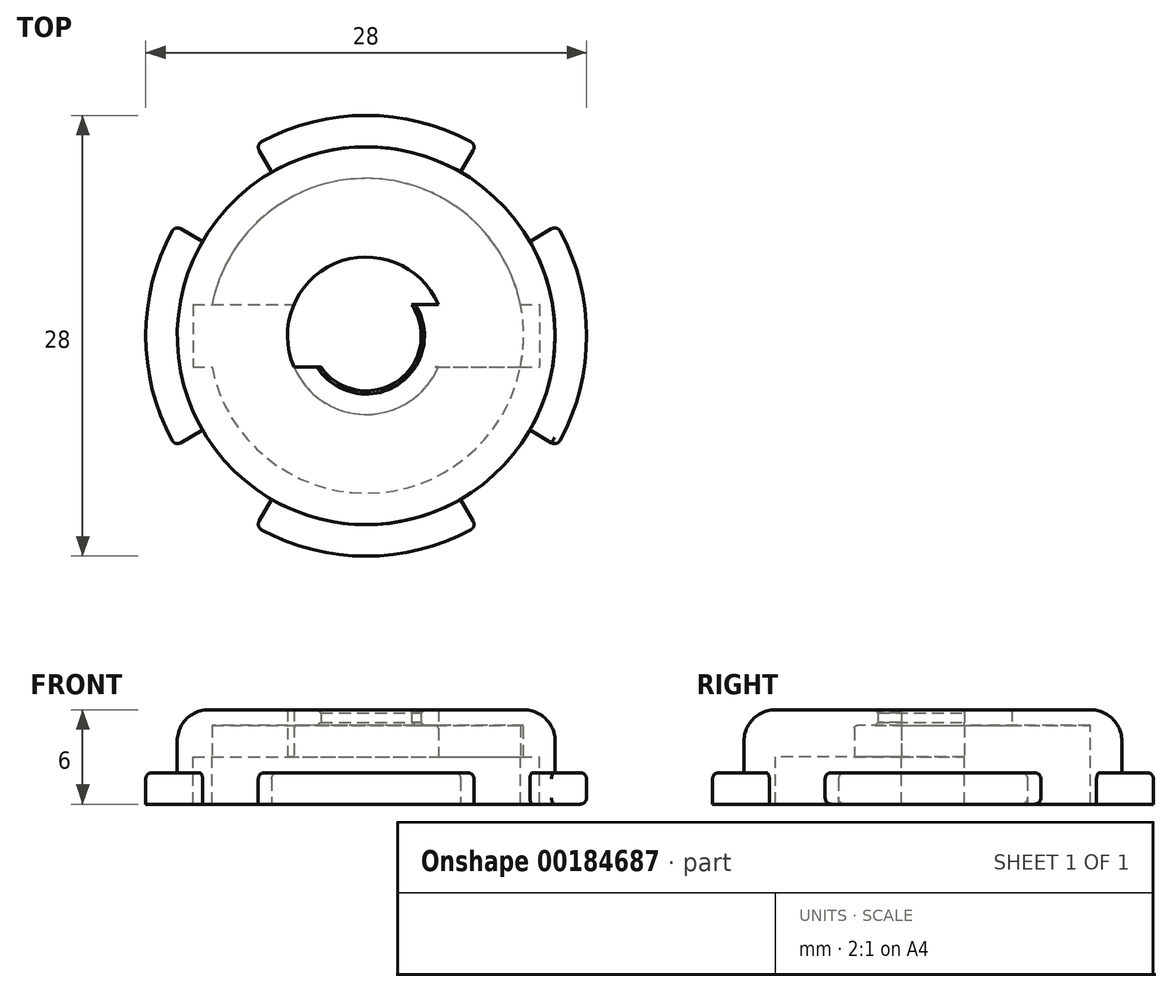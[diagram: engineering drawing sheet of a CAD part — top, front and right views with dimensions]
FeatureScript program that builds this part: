
annotation { "Feature Type Name" : "Feature", "Feature Type Description" : "" }
export const myFeature = defineFeature(function(context is Context, id is Id, definition is map)
    precondition{}
    {
        {
            var Q0;
            Q0=qCreatedBy(makeId("Top.planeOp"),FACE);
            var sketch = newSketch(context, id + "F0", { "sketchPlane" : qUnion([Q0])});
            skCircle(sketch, "E0", {"center": v(0, 0) * mm, "radius": 10 * mm});
            skLineSegment(sketch, "E1.bottom", {"start": v(-11, 2) * mm, "end": v(11, 2) * mm});
            skLineSegment(sketch, "E1.top", {"start": v(-11, -2) * mm, "end": v(11, -2) * mm});
            skLineSegment(sketch, "E1.left", {"start": v(-11, 2) * mm, "end": v(-11, -2) * mm});
            skLineSegment(sketch, "E1.right", {"start": v(11, 2) * mm, "end": v(11, -2) * mm});
            skCircle(sketch, "E2", {"center": v(0, 0) * mm, "radius": 12 * mm});
            skCircle(sketch, "E3", {"center": v(0, 0) * mm, "radius": 3.5 * mm});
            skCircle(sketch, "E4", {"center": v(0, 0) * mm, "radius": 5 * mm});
            skSolve(sketch);
        }
        {
            var Q0;
            {var subQ4=sQuery(id+"F0.wireOp",EDGE,"E1.left");Q0=makeQuery(id+"F0.imprint","IMPRINT",FACE,{"disambiguationData":[TD([[makeQuery(id+"F0.imprint","IMPRINT",EDGE,{"derivedFrom":subQ4}),-1.0]])]});}
            var Q1;
            {var subQ5=sQuery(id+"F0.wireOp",EDGE,"E1.left");Q1=makeQuery(id+"F0.imprint","IMPRINT",FACE,{"disambiguationData":[TD([[makeQuery(id+"F0.imprint","IMPRINT",EDGE,{"derivedFrom":subQ5}),1.0]])]});}
            var Q2;
            {var subQ0=sQuery(id+"F0.wireOp",EDGE,"E1.top");var subQ1=sQuery(id+"F0.wireOp",EDGE,"E0");var subQ2=makeQuery(id+"F0.imprint","INTERSECT",VERTEX,{"disambiguationData":[OD(0.0)],"derivedFrom":[subQ1,subQ0]});Q2=makeQuery(id+"F0.imprint","IMPRINT",FACE,{"disambiguationData":[TD([[makeQuery(id+"F0.imprint","IMPRINT",EDGE,{"disambiguationData":[TD([[subQ2,-1.0]])],"derivedFrom":subQ1}),1.0]])]});}
            var Q3;
            {var subQ0=sQuery(id+"F0.wireOp",EDGE,"E1.bottom");var subQ1=sQuery(id+"F0.wireOp",EDGE,"E0");var subQ2=makeQuery(id+"F0.imprint","INTERSECT",VERTEX,{"disambiguationData":[OD(0.0)],"derivedFrom":[subQ1,subQ0]});Q3=makeQuery(id+"F0.imprint","IMPRINT",FACE,{"disambiguationData":[TD([[makeQuery(id+"F0.imprint","IMPRINT",EDGE,{"disambiguationData":[TD([[subQ2,-1.0]])],"derivedFrom":subQ1}),1.0]])]});}
            var Q4;
            {var subQ0=sQuery(id+"F0.wireOp",EDGE,"E1.bottom");var subQ1=sQuery(id+"F0.wireOp",EDGE,"E0");var subQ2=makeQuery(id+"F0.imprint","INTERSECT",VERTEX,{"disambiguationData":[OD(0.0)],"derivedFrom":[subQ1,subQ0]});Q4=makeQuery(id+"F0.imprint","IMPRINT",FACE,{"disambiguationData":[TD([[makeQuery(id+"F0.imprint","IMPRINT",EDGE,{"disambiguationData":[TD([[subQ2,1.0]])],"derivedFrom":subQ1}),1.0]])]});}
            var Q5;
            {var subQ5=sQuery(id+"F0.wireOp",EDGE,"E1.right");Q5=makeQuery(id+"F0.imprint","IMPRINT",FACE,{"disambiguationData":[TD([[makeQuery(id+"F0.imprint","IMPRINT",EDGE,{"derivedFrom":subQ5}),-1.0]])]});}
            var Q6;
            {var subQ0=sQuery(id+"F0.wireOp",EDGE,"E1.bottom");var subQ1=sQuery(id+"F0.wireOp",EDGE,"E0");var subQ2=makeQuery(id+"F0.imprint","INTERSECT",VERTEX,{"disambiguationData":[OD(1.0)],"derivedFrom":[subQ1,subQ0]});Q6=makeQuery(id+"F0.imprint","IMPRINT",FACE,{"disambiguationData":[TD([[makeQuery(id+"F0.imprint","IMPRINT",EDGE,{"disambiguationData":[TD([[subQ2,1.0]])],"derivedFrom":subQ1}),1.0]])]});}
            var Q7;
            {var subQ0=sQuery(id+"F0.wireOp",EDGE,"E4");var subQ1=sQuery(id+"F0.wireOp",EDGE,"E1.top");var subQ2=makeQuery(id+"F0.imprint","INTERSECT",VERTEX,{"disambiguationData":[OD(0.0)],"derivedFrom":[subQ1,subQ0]});Q7=makeQuery(id+"F0.imprint","IMPRINT",FACE,{"disambiguationData":[TD([[makeQuery(id+"F0.imprint","IMPRINT",EDGE,{"disambiguationData":[TD([[subQ2,-1.0]])],"derivedFrom":subQ1}),-1.0]])]});}
            var Q8;
            {var subQ0=sQuery(id+"F0.wireOp",EDGE,"E4");var subQ1=sQuery(id+"F0.wireOp",EDGE,"E1.bottom");var subQ2=makeQuery(id+"F0.imprint","INTERSECT",VERTEX,{"disambiguationData":[OD(0.0)],"derivedFrom":[subQ1,subQ0]});Q8=makeQuery(id+"F0.imprint","IMPRINT",FACE,{"disambiguationData":[TD([[makeQuery(id+"F0.imprint","IMPRINT",EDGE,{"disambiguationData":[TD([[subQ2,-1.0]])],"derivedFrom":subQ1}),-1.0]])]});}
            var Q9;
            {var subQ0=sQuery(id+"F0.wireOp",EDGE,"E3");var subQ1=sQuery(id+"F0.wireOp",EDGE,"E1.top");var subQ2=makeQuery(id+"F0.imprint","INTERSECT",VERTEX,{"disambiguationData":[OD(0.0)],"derivedFrom":[subQ1,subQ0]});Q9=makeQuery(id+"F0.imprint","IMPRINT",FACE,{"disambiguationData":[TD([[makeQuery(id+"F0.imprint","IMPRINT",EDGE,{"disambiguationData":[TD([[subQ2,-1.0]])],"derivedFrom":subQ1}),-1.0]])]});}
            var Q10;
            {var subQ0=sQuery(id+"F0.wireOp",EDGE,"E3");var subQ1=sQuery(id+"F0.wireOp",EDGE,"E1.bottom");var subQ2=makeQuery(id+"F0.imprint","INTERSECT",VERTEX,{"disambiguationData":[OD(0.0)],"derivedFrom":[subQ1,subQ0]});Q10=makeQuery(id+"F0.imprint","IMPRINT",FACE,{"disambiguationData":[TD([[makeQuery(id+"F0.imprint","IMPRINT",EDGE,{"disambiguationData":[TD([[subQ2,-1.0]])],"derivedFrom":subQ1}),1.0]])]});}
            var Q11;
            {var subQ0=sQuery(id+"F0.wireOp",EDGE,"E4");var subQ1=sQuery(id+"F0.wireOp",EDGE,"E1.bottom");var subQ2=makeQuery(id+"F0.imprint","INTERSECT",VERTEX,{"disambiguationData":[OD(0.0)],"derivedFrom":[subQ1,subQ0]});Q11=makeQuery(id+"F0.imprint","IMPRINT",FACE,{"disambiguationData":[TD([[makeQuery(id+"F0.imprint","IMPRINT",EDGE,{"disambiguationData":[TD([[subQ2,-1.0]])],"derivedFrom":subQ1}),1.0]])]});}
            var Q12;
            {var subQ0=sQuery(id+"F0.wireOp",EDGE,"E3");var subQ1=sQuery(id+"F0.wireOp",EDGE,"E1.bottom");var subQ2=makeQuery(id+"F0.imprint","INTERSECT",VERTEX,{"disambiguationData":[OD(1.0)],"derivedFrom":[subQ1,subQ0]});Q12=makeQuery(id+"F0.imprint","IMPRINT",FACE,{"disambiguationData":[TD([[makeQuery(id+"F0.imprint","IMPRINT",EDGE,{"disambiguationData":[TD([[subQ2,-1.0]])],"derivedFrom":subQ1}),-1.0]])]});}
            var Q13;
            {var subQ0=sQuery(id+"F0.wireOp",EDGE,"E3");var subQ1=sQuery(id+"F0.wireOp",EDGE,"E1.bottom");var subQ2=makeQuery(id+"F0.imprint","INTERSECT",VERTEX,{"disambiguationData":[OD(0.0)],"derivedFrom":[subQ1,subQ0]});Q13=makeQuery(id+"F0.imprint","IMPRINT",FACE,{"disambiguationData":[TD([[makeQuery(id+"F0.imprint","IMPRINT",EDGE,{"disambiguationData":[TD([[subQ2,-1.0]])],"derivedFrom":subQ1}),-1.0]])]});}
            extrude(context, id + "F1", {"entities" : qUnion([Q0, Q1, Q2, Q3, Q4, Q5, Q6, Q7, Q8, Q9, Q10, Q11, Q12, Q13]), "depth" : 3 * mm});
        }
        {
            var Q0;
            {var subQ4=sQuery(id+"F0.wireOp",EDGE,"E1.left");Q0=makeQuery(id+"F0.imprint","IMPRINT",FACE,{"disambiguationData":[TD([[makeQuery(id+"F0.imprint","IMPRINT",EDGE,{"derivedFrom":subQ4}),-1.0]])]});}
            extrude(context, id + "F2", {"entities" : qUnion([Q0]), "operationType" : NewBodyOperationType.ADD, "oppositeDirection" : true, "depth" : 3 * mm});
        }
        {
            var Q0;
            Q0=makeQuery(id+"F1.opExtrude","CAP_EDGE",EDGE,{"disambiguationData":[OSD([sQuery(id+"F0.wireOp",EDGE,"E2")])],"isStart":false});
            fillet(context, id + "F3", {"entities" : qUnion([Q0]), "radius" : 2 * mm, "tangentPropagation" : true, "allowEdgeOverflow" : false});
        }
        {
            var Q0;
            Q0=qCreatedBy(makeId("Top.planeOp"),FACE);
            var sketch = newSketch(context, id + "F4", { "sketchPlane" : qUnion([Q0])});
            skLineSegment(sketch, "E5.bottom", {"start": v(-6.5, -2) * mm, "end": v(-3.5, -2) * mm});
            skLineSegment(sketch, "E5.top", {"start": v(-6.5, 2) * mm, "end": v(-3.5, 2) * mm});
            skLineSegment(sketch, "E5.left", {"start": v(-6.5, -2) * mm, "end": v(-6.5, 2) * mm});
            skLineSegment(sketch, "E5.right", {"start": v(-3.5, -2) * mm, "end": v(-3.5, 2) * mm});
            skLineSegment(sketch, "E6.bottom", {"start": v(3.5, -2) * mm, "end": v(6.5, -2) * mm});
            skLineSegment(sketch, "E6.top", {"start": v(3.5, 2) * mm, "end": v(6.5, 2) * mm});
            skLineSegment(sketch, "E6.left", {"start": v(3.5, -2) * mm, "end": v(3.5, 2) * mm});
            skLineSegment(sketch, "E6.right", {"start": v(6.5, -2) * mm, "end": v(6.5, 2) * mm});
            skCircle(sketch, "E7", {"center": v(0, 0) * mm, "radius": 9.5 * mm});
            skCircle(sketch, "E8", {"center": v(0, 0) * mm, "radius": 5 * mm});
            skSolve(sketch);
        }
        {
            var Q0;
            {var subQ0=sQuery(id+"F0.wireOp",EDGE,"E4");var subQ1=sQuery(id+"F0.wireOp",EDGE,"E1.top");var subQ2=makeQuery(id+"F0.imprint","INTERSECT",VERTEX,{"disambiguationData":[OD(0.0)],"derivedFrom":[subQ1,subQ0]});Q0=makeQuery(id+"F0.imprint","IMPRINT",FACE,{"disambiguationData":[TD([[makeQuery(id+"F0.imprint","IMPRINT",EDGE,{"disambiguationData":[TD([[subQ2,-1.0]])],"derivedFrom":subQ1}),-1.0]])]});}
            var Q1;
            {var subQ0=sQuery(id+"F0.wireOp",EDGE,"E3");var subQ1=sQuery(id+"F0.wireOp",EDGE,"E1.bottom");var subQ2=makeQuery(id+"F0.imprint","INTERSECT",VERTEX,{"disambiguationData":[OD(1.0)],"derivedFrom":[subQ1,subQ0]});Q1=makeQuery(id+"F0.imprint","IMPRINT",FACE,{"disambiguationData":[TD([[makeQuery(id+"F0.imprint","IMPRINT",EDGE,{"disambiguationData":[TD([[subQ2,-1.0]])],"derivedFrom":subQ1}),-1.0]])]});}
            var Q2;
            {var subQ0=sQuery(id+"F0.wireOp",EDGE,"E4");var subQ1=sQuery(id+"F0.wireOp",EDGE,"E1.bottom");var subQ2=makeQuery(id+"F0.imprint","INTERSECT",VERTEX,{"disambiguationData":[OD(0.0)],"derivedFrom":[subQ1,subQ0]});Q2=makeQuery(id+"F0.imprint","IMPRINT",FACE,{"disambiguationData":[TD([[makeQuery(id+"F0.imprint","IMPRINT",EDGE,{"disambiguationData":[TD([[subQ2,-1.0]])],"derivedFrom":subQ1}),1.0]])]});}
            var Q3;
            {var subQ0=sQuery(id+"F0.wireOp",EDGE,"E4");var subQ1=sQuery(id+"F0.wireOp",EDGE,"E1.bottom");var subQ2=makeQuery(id+"F0.imprint","INTERSECT",VERTEX,{"disambiguationData":[OD(0.0)],"derivedFrom":[subQ1,subQ0]});Q3=makeQuery(id+"F0.imprint","IMPRINT",FACE,{"disambiguationData":[TD([[makeQuery(id+"F0.imprint","IMPRINT",EDGE,{"disambiguationData":[TD([[subQ2,-1.0]])],"derivedFrom":subQ1}),-1.0]])]});}
            var Q4;
            {var subQ0=sQuery(id+"F0.wireOp",EDGE,"E3");var subQ1=sQuery(id+"F0.wireOp",EDGE,"E1.bottom");var subQ2=makeQuery(id+"F0.imprint","INTERSECT",VERTEX,{"disambiguationData":[OD(0.0)],"derivedFrom":[subQ1,subQ0]});Q4=makeQuery(id+"F0.imprint","IMPRINT",FACE,{"disambiguationData":[TD([[makeQuery(id+"F0.imprint","IMPRINT",EDGE,{"disambiguationData":[TD([[subQ2,-1.0]])],"derivedFrom":subQ1}),1.0]])]});}
            var Q5;
            {var subQ0=sQuery(id+"F4.wireOp",EDGE,"E5.right");Q5=makeQuery(id+"F4.imprint","IMPRINT",FACE,{"disambiguationData":[TD([[makeQuery(id+"F4.imprint","IMPRINT",EDGE,{"derivedFrom":subQ0}),1.0]])]});}
            var Q6;
            {var subQ0=sQuery(id+"F0.wireOp",EDGE,"E3");var subQ1=sQuery(id+"F0.wireOp",EDGE,"E1.top");var subQ2=makeQuery(id+"F0.imprint","INTERSECT",VERTEX,{"disambiguationData":[OD(0.0)],"derivedFrom":[subQ1,subQ0]});Q6=makeQuery(id+"F0.imprint","IMPRINT",FACE,{"disambiguationData":[TD([[makeQuery(id+"F0.imprint","IMPRINT",EDGE,{"disambiguationData":[TD([[subQ2,-1.0]])],"derivedFrom":subQ1}),-1.0]])]});}
            var Q7;
            {var subQ0=sQuery(id+"F4.wireOp",EDGE,"E6.left");Q7=makeQuery(id+"F4.imprint","IMPRINT",FACE,{"disambiguationData":[TD([[makeQuery(id+"F4.imprint","IMPRINT",EDGE,{"derivedFrom":subQ0}),-1.0]])]});}
            var Q8;
            {var subQ0=sQuery(id+"F0.wireOp",EDGE,"E3");var subQ1=sQuery(id+"F0.wireOp",EDGE,"E1.bottom");var subQ2=makeQuery(id+"F0.imprint","INTERSECT",VERTEX,{"disambiguationData":[OD(0.0)],"derivedFrom":[subQ1,subQ0]});Q8=makeQuery(id+"F0.imprint","IMPRINT",FACE,{"disambiguationData":[TD([[makeQuery(id+"F0.imprint","IMPRINT",EDGE,{"disambiguationData":[TD([[subQ2,-1.0]])],"derivedFrom":subQ1}),-1.0]])]});}
            extrude(context, id + "F5", {"entities" : qUnion([Q0, Q1, Q2, Q3, Q4, Q5, Q6, Q7, Q8]), "operationType" : NewBodyOperationType.REMOVE, "depth" : 2 * mm});
        }
        {
            var Q0;
            Q0=makeQuery(id+"F2.opExtrude","CAP_FACE",FACE,{"disambiguationData":[OSD([sQuery(id+"F0.wireOp",EDGE,"E0"),sQuery(id+"F0.wireOp",EDGE,"E1.bottom"),sQuery(id+"F0.wireOp",EDGE,"E1.top"),sQuery(id+"F0.wireOp",EDGE,"E1.left"),sQuery(id+"F0.wireOp",EDGE,"E1.right"),sQuery(id+"F0.wireOp",EDGE,"E2")])],"isStart":false});
            var sketch = newSketch(context, id + "F6", { "sketchPlane" : qUnion([Q0])});
            skCircle(sketch, "E9", {"center": v(0, 0) * mm, "radius": 14 * mm});
            skLineSegment(sketch, "E10", {"start": v(0, 0) * mm, "end": v(-12.12, -7) * mm});
            skLineSegment(sketch, "E11", {"start": v(-7, -12.12) * mm, "end": v(0, 0) * mm});
            skPoint(sketch, "E12.orphan", {"position": v(14.5, 8.38) * mm});
            skPoint(sketch, "E13.orphan", {"position": v(8.38, -14.5) * mm});
            skPoint(sketch, "E14.orphan", {"position": v(-8.2, -14.2) * mm});
            skPoint(sketch, "E15.orphan", {"position": v(-14.5, -8.38) * mm});
            skPoint(sketch, "E16.orphan", {"position": v(-14.2, 8.2) * mm});
            skCircle(sketch, "E17", {"center": v(0, 0) * mm, "radius": 16 * mm});
            skCircle(sketch, "E18", {"center": v(0, 0) * mm, "radius": 12 * mm});
            skLineSegment(sketch, "E19.1.0", {"start": v(12.12, -7) * mm, "end": v(0, 0) * mm});
            skLineSegment(sketch, "E19.1.1", {"start": v(0, 0) * mm, "end": v(7, -12.12) * mm});
            skLineSegment(sketch, "E19.2.0", {"start": v(7, 12.12) * mm, "end": v(0, 0) * mm});
            skLineSegment(sketch, "E19.2.1", {"start": v(0, 0) * mm, "end": v(12.12, 7) * mm});
            skLineSegment(sketch, "E19.3.0", {"start": v(-12.12, 7) * mm, "end": v(0, 0) * mm});
            skLineSegment(sketch, "E19.3.1", {"start": v(0, 0) * mm, "end": v(-7, 12.12) * mm});
            skSolve(sketch);
        }
        {
            var Q0;
            {var subQ0=sQuery(id+"F6.wireOp",EDGE,"E10");var subQ1=sQuery(id+"F6.wireOp",EDGE,"E9");var subQ2=makeQuery(id+"F6.imprint","INTERSECT",VERTEX,{"derivedFrom":[subQ1,subQ0]});Q0=makeQuery(id+"F6.imprint","IMPRINT",FACE,{"disambiguationData":[TD([[makeQuery(id+"F6.imprint","IMPRINT",EDGE,{"disambiguationData":[TD([[subQ2,1.0]])],"derivedFrom":subQ1}),1.0]])]});}
            var Q1;
            {var subQ0=sQuery(id+"F6.wireOp",EDGE,"E19.2.0");var subQ1=sQuery(id+"F6.wireOp",EDGE,"E9");var subQ2=makeQuery(id+"F6.imprint","INTERSECT",VERTEX,{"derivedFrom":[subQ1,subQ0]});Q1=makeQuery(id+"F6.imprint","IMPRINT",FACE,{"disambiguationData":[TD([[makeQuery(id+"F6.imprint","IMPRINT",EDGE,{"disambiguationData":[TD([[subQ2,-1.0]])],"derivedFrom":subQ1}),1.0]])]});}
            var Q2;
            {var subQ0=sQuery(id+"F6.wireOp",EDGE,"E19.1.0");var subQ1=sQuery(id+"F6.wireOp",EDGE,"E9");var subQ2=makeQuery(id+"F6.imprint","INTERSECT",VERTEX,{"derivedFrom":[subQ1,subQ0]});Q2=makeQuery(id+"F6.imprint","IMPRINT",FACE,{"disambiguationData":[TD([[makeQuery(id+"F6.imprint","IMPRINT",EDGE,{"disambiguationData":[TD([[subQ2,-1.0]])],"derivedFrom":subQ1}),1.0]])]});}
            var Q3;
            {var subQ0=sQuery(id+"F6.wireOp",EDGE,"E11");var subQ1=sQuery(id+"F6.wireOp",EDGE,"E9");var subQ2=makeQuery(id+"F6.imprint","INTERSECT",VERTEX,{"derivedFrom":[subQ1,subQ0]});Q3=makeQuery(id+"F6.imprint","IMPRINT",FACE,{"disambiguationData":[TD([[makeQuery(id+"F6.imprint","IMPRINT",EDGE,{"disambiguationData":[TD([[subQ2,-1.0]])],"derivedFrom":subQ1}),1.0]])]});}
            extrude(context, id + "F7", {"entities" : qUnion([Q0, Q1, Q2, Q3]), "operationType" : NewBodyOperationType.ADD, "oppositeDirection" : true, "depth" : 2 * mm});
        }
        {
            var Q0;
            Q0=makeQuery(id+"F7.opExtrude","SWEPT_EDGE",EDGE,{"disambiguationData":[OSD([sQuery(id+"F6.wireOp",EDGE,"E18"),sQuery(id+"F6.wireOp",EDGE,"E19.2.1")])]});
            var Q1;
            Q1=makeQuery(id+"F7.opExtrude","SWEPT_EDGE",EDGE,{"disambiguationData":[OSD([sQuery(id+"F6.wireOp",EDGE,"E18"),sQuery(id+"F6.wireOp",EDGE,"E19.2.0")])]});
            var Q2;
            Q2=makeQuery(id+"F7.opExtrude","SWEPT_EDGE",EDGE,{"disambiguationData":[OSD([sQuery(id+"F6.wireOp",EDGE,"E9"),sQuery(id+"F6.wireOp",EDGE,"E19.2.1")])]});
            var Q3;
            Q3=makeQuery(id+"F7.opExtrude","SWEPT_EDGE",EDGE,{"disambiguationData":[OSD([sQuery(id+"F6.wireOp",EDGE,"E9"),sQuery(id+"F6.wireOp",EDGE,"E19.2.0")])]});
            var Q4;
            Q4=makeQuery(id+"F7.opExtrude","SWEPT_EDGE",EDGE,{"disambiguationData":[OSD([sQuery(id+"F6.wireOp",EDGE,"E9"),sQuery(id+"F6.wireOp",EDGE,"E19.3.1")])]});
            var Q5;
            Q5=makeQuery(id+"F7.opExtrude","SWEPT_EDGE",EDGE,{"disambiguationData":[OSD([sQuery(id+"F6.wireOp",EDGE,"E9"),sQuery(id+"F6.wireOp",EDGE,"E19.3.0")])]});
            var Q6;
            Q6=makeQuery(id+"F7.opExtrude","SWEPT_EDGE",EDGE,{"disambiguationData":[OSD([sQuery(id+"F6.wireOp",EDGE,"E18"),sQuery(id+"F6.wireOp",EDGE,"E19.3.1")])]});
            var Q7;
            Q7=makeQuery(id+"F7.opExtrude","SWEPT_EDGE",EDGE,{"disambiguationData":[OSD([sQuery(id+"F6.wireOp",EDGE,"E18"),sQuery(id+"F6.wireOp",EDGE,"E19.3.0")])]});
            var Q8;
            Q8=makeQuery(id+"F7.opExtrude","SWEPT_EDGE",EDGE,{"disambiguationData":[OSD([sQuery(id+"F6.wireOp",EDGE,"E10"),sQuery(id+"F6.wireOp",EDGE,"E18")])]});
            var Q9;
            Q9=makeQuery(id+"F7.opExtrude","SWEPT_EDGE",EDGE,{"disambiguationData":[OSD([sQuery(id+"F6.wireOp",EDGE,"E9"),sQuery(id+"F6.wireOp",EDGE,"E10")])]});
            var Q10;
            Q10=makeQuery(id+"F7.opExtrude","SWEPT_EDGE",EDGE,{"disambiguationData":[OSD([sQuery(id+"F6.wireOp",EDGE,"E11"),sQuery(id+"F6.wireOp",EDGE,"E18")])]});
            var Q11;
            Q11=makeQuery(id+"F7.opExtrude","SWEPT_EDGE",EDGE,{"disambiguationData":[OSD([sQuery(id+"F6.wireOp",EDGE,"E9"),sQuery(id+"F6.wireOp",EDGE,"E11")])]});
            var Q12;
            Q12=makeQuery(id+"F7.opExtrude","SWEPT_EDGE",EDGE,{"disambiguationData":[OSD([sQuery(id+"F6.wireOp",EDGE,"E18"),sQuery(id+"F6.wireOp",EDGE,"E19.1.1")])]});
            var Q13;
            Q13=makeQuery(id+"F7.opExtrude","SWEPT_EDGE",EDGE,{"disambiguationData":[OSD([sQuery(id+"F6.wireOp",EDGE,"E9"),sQuery(id+"F6.wireOp",EDGE,"E19.1.1")])]});
            var Q14;
            Q14=makeQuery(id+"F7.opExtrude","SWEPT_EDGE",EDGE,{"disambiguationData":[OSD([sQuery(id+"F6.wireOp",EDGE,"E18"),sQuery(id+"F6.wireOp",EDGE,"E19.1.0")])]});
            var Q15;
            Q15=makeQuery(id+"F7.opExtrude","SWEPT_EDGE",EDGE,{"disambiguationData":[OSD([sQuery(id+"F6.wireOp",EDGE,"E9"),sQuery(id+"F6.wireOp",EDGE,"E19.1.0")])]});
            fillet(context, id + "F8", {"entities" : qUnion([Q0, Q1, Q2, Q3, Q4, Q5, Q6, Q7, Q8, Q9, Q10, Q11, Q12, Q13, Q14, Q15]), "radius" : 0.4 * mm, "tangentPropagation" : true, "allowEdgeOverflow" : false});
        }
        {
            var Q0;
            {var subQ0=sQuery(id+"F6.wireOp",EDGE,"E9");Q0=makeQuery(id+"F7.opExtrude","CAP_EDGE",EDGE,{"disambiguationData":[OSD([subQ0]),TDD([makeQuery(id+"F6.imprint","IMPRINT",EDGE,{"disambiguationData":[TD([[makeQuery(id+"F6.imprint","INTERSECT",VERTEX,{"derivedFrom":[subQ0,sQuery(id+"F6.wireOp",EDGE,"E19.1.0")]}),-1.0]])],"derivedFrom":subQ0})])],"isStart":true});}
            var Q1;
            {var subQ0=sQuery(id+"F6.wireOp",EDGE,"E9");Q1=makeQuery(id+"F7.opExtrude","CAP_EDGE",EDGE,{"disambiguationData":[OSD([subQ0]),TDD([makeQuery(id+"F6.imprint","IMPRINT",EDGE,{"disambiguationData":[TD([[makeQuery(id+"F6.imprint","INTERSECT",VERTEX,{"derivedFrom":[subQ0,sQuery(id+"F6.wireOp",EDGE,"E19.1.0")]}),-1.0]])],"derivedFrom":subQ0})])],"isStart":false});}
            var Q2;
            {var subQ0=sQuery(id+"F6.wireOp",EDGE,"E9");Q2=makeQuery(id+"F7.opExtrude","CAP_EDGE",EDGE,{"disambiguationData":[OSD([subQ0]),TDD([makeQuery(id+"F6.imprint","IMPRINT",EDGE,{"disambiguationData":[TD([[makeQuery(id+"F6.imprint","INTERSECT",VERTEX,{"derivedFrom":[subQ0,sQuery(id+"F6.wireOp",EDGE,"E11")]}),-1.0]])],"derivedFrom":subQ0})])],"isStart":false});}
            var Q3;
            {var subQ0=sQuery(id+"F6.wireOp",EDGE,"E9");Q3=makeQuery(id+"F7.opExtrude","CAP_EDGE",EDGE,{"disambiguationData":[OSD([subQ0]),TDD([makeQuery(id+"F6.imprint","IMPRINT",EDGE,{"disambiguationData":[TD([[makeQuery(id+"F6.imprint","INTERSECT",VERTEX,{"derivedFrom":[subQ0,sQuery(id+"F6.wireOp",EDGE,"E10")]}),1.0]])],"derivedFrom":subQ0})])],"isStart":false});}
            var Q4;
            {var subQ0=sQuery(id+"F6.wireOp",EDGE,"E9");Q4=makeQuery(id+"F7.opExtrude","CAP_EDGE",EDGE,{"disambiguationData":[OSD([subQ0]),TDD([makeQuery(id+"F6.imprint","IMPRINT",EDGE,{"disambiguationData":[TD([[makeQuery(id+"F6.imprint","INTERSECT",VERTEX,{"derivedFrom":[subQ0,sQuery(id+"F6.wireOp",EDGE,"E19.2.0")]}),-1.0]])],"derivedFrom":subQ0})])],"isStart":false});}
            var Q5;
            {var subQ0=sQuery(id+"F6.wireOp",EDGE,"E18");Q5=makeQuery(id+"F7.opExtrude","CAP_EDGE",EDGE,{"disambiguationData":[OSD([subQ0]),TDD([makeQuery(id+"F6.imprint","IMPRINT",EDGE,{"disambiguationData":[TD([[makeQuery(id+"F6.imprint","INTERSECT",VERTEX,{"derivedFrom":[subQ0,sQuery(id+"F6.wireOp",EDGE,"E19.1.0")]}),1.0]])],"derivedFrom":subQ0})])],"isStart":false});}
            var Q6;
            {var subQ0=sQuery(id+"F6.wireOp",EDGE,"E18");Q6=makeQuery(id+"F7.opExtrude","CAP_EDGE",EDGE,{"disambiguationData":[OSD([subQ0]),TDD([makeQuery(id+"F6.imprint","IMPRINT",EDGE,{"disambiguationData":[TD([[makeQuery(id+"F6.imprint","INTERSECT",VERTEX,{"derivedFrom":[subQ0,sQuery(id+"F6.wireOp",EDGE,"E19.3.1")]}),-1.0]])],"derivedFrom":subQ0})])],"isStart":false});}
            var Q7;
            {var subQ0=sQuery(id+"F6.wireOp",EDGE,"E18");Q7=makeQuery(id+"F7.opExtrude","CAP_EDGE",EDGE,{"disambiguationData":[OSD([subQ0]),TDD([makeQuery(id+"F6.imprint","IMPRINT",EDGE,{"disambiguationData":[TD([[makeQuery(id+"F6.imprint","INTERSECT",VERTEX,{"derivedFrom":[sQuery(id+"F6.wireOp",EDGE,"E11"),subQ0]}),1.0]])],"derivedFrom":subQ0})])],"isStart":false});}
            var Q8;
            {var subQ0=sQuery(id+"F6.wireOp",EDGE,"E18");Q8=makeQuery(id+"F7.opExtrude","CAP_EDGE",EDGE,{"disambiguationData":[OSD([subQ0]),TDD([makeQuery(id+"F6.imprint","IMPRINT",EDGE,{"disambiguationData":[TD([[makeQuery(id+"F6.imprint","INTERSECT",VERTEX,{"derivedFrom":[sQuery(id+"F6.wireOp",EDGE,"E10"),subQ0]}),-1.0]])],"derivedFrom":subQ0})])],"isStart":false});}
            fillet(context, id + "F9", {"entities" : qUnion([Q0, Q1, Q2, Q3, Q4, Q5, Q6, Q7, Q8]), "radius" : 0.4 * mm, "tangentPropagation" : true, "allowEdgeOverflow" : false});
        }
        {
            var Q0;
            Q0=makeQuery(id+"F5.boolean.opBoolean","COPY",EDGE,{"derivedFrom":makeQuery(id+"F5.opExtrude","CAP_EDGE",EDGE,{"disambiguationData":[OSD([sQuery(id+"F0.wireOp",EDGE,"E4")])],"isStart":false})});
            fillet(context, id + "F10", {"entities" : qUnion([Q0]), "radius" : 0.2 * mm, "tangentPropagation" : true, "allowEdgeOverflow" : false});
        }
        {
            var Q0;
            {var subQ0=sQuery(id+"F0.wireOp",EDGE,"E3");var subQ1=sQuery(id+"F0.wireOp",EDGE,"E1.top");var subQ2=makeQuery(id+"F0.imprint","INTERSECT",VERTEX,{"disambiguationData":[OD(0.0)],"derivedFrom":[subQ1,subQ0]});Q0=makeQuery(id+"F0.imprint","IMPRINT",FACE,{"disambiguationData":[TD([[makeQuery(id+"F0.imprint","IMPRINT",EDGE,{"disambiguationData":[TD([[subQ2,-1.0]])],"derivedFrom":subQ1}),-1.0]])]});}
            var Q1;
            {var subQ0=sQuery(id+"F0.wireOp",EDGE,"E3");var subQ1=sQuery(id+"F0.wireOp",EDGE,"E1.bottom");var subQ2=makeQuery(id+"F0.imprint","INTERSECT",VERTEX,{"disambiguationData":[OD(0.0)],"derivedFrom":[subQ1,subQ0]});Q1=makeQuery(id+"F0.imprint","IMPRINT",FACE,{"disambiguationData":[TD([[makeQuery(id+"F0.imprint","IMPRINT",EDGE,{"disambiguationData":[TD([[subQ2,-1.0]])],"derivedFrom":subQ1}),-1.0]])]});}
            var Q2;
            {var subQ0=sQuery(id+"F0.wireOp",EDGE,"E3");var subQ1=sQuery(id+"F0.wireOp",EDGE,"E1.bottom");var subQ2=makeQuery(id+"F0.imprint","INTERSECT",VERTEX,{"disambiguationData":[OD(0.0)],"derivedFrom":[subQ1,subQ0]});Q2=makeQuery(id+"F0.imprint","IMPRINT",FACE,{"disambiguationData":[TD([[makeQuery(id+"F0.imprint","IMPRINT",EDGE,{"disambiguationData":[TD([[subQ2,-1.0]])],"derivedFrom":subQ1}),1.0]])]});}
            extrude(context, id + "F11", {"entities" : qUnion([Q0, Q1, Q2]), "operationType" : NewBodyOperationType.REMOVE, "depth" : 25 * mm});
        }
        {
            var Q0;
            Q0=makeQuery(id+"F11.boolean.opBoolean","INTERSECT",EDGE,{"derivedFrom":[makeQuery(id+"F5.boolean.opBoolean","COPY",FACE,{"derivedFrom":makeQuery(id+"F5.opExtrude","CAP_FACE",FACE,{"disambiguationData":[OSD([sQuery(id+"F0.wireOp",EDGE,"E4")])],"isStart":false})}),makeQuery(id+"F11.opExtrude","SWEPT_FACE",FACE,{"disambiguationData":[OSD([sQuery(id+"F0.wireOp",EDGE,"E3")])]})]});
            var Q1;
            Q1=makeQuery(id+"F11.boolean.opBoolean","INTERSECT",EDGE,{"derivedFrom":[makeQuery(id+"F1.opExtrude","CAP_FACE",FACE,{"disambiguationData":[OSD([sQuery(id+"F0.wireOp",EDGE,"E2")])],"isStart":false}),makeQuery(id+"F11.opExtrude","SWEPT_FACE",FACE,{"disambiguationData":[OSD([sQuery(id+"F0.wireOp",EDGE,"E3")])]})]});
            chamfer(context, id + "F12", {"entities" : qUnion([Q0, Q1]), "width" : 0.2 * mm, "tangentPropagation" : true});
        }
    });
